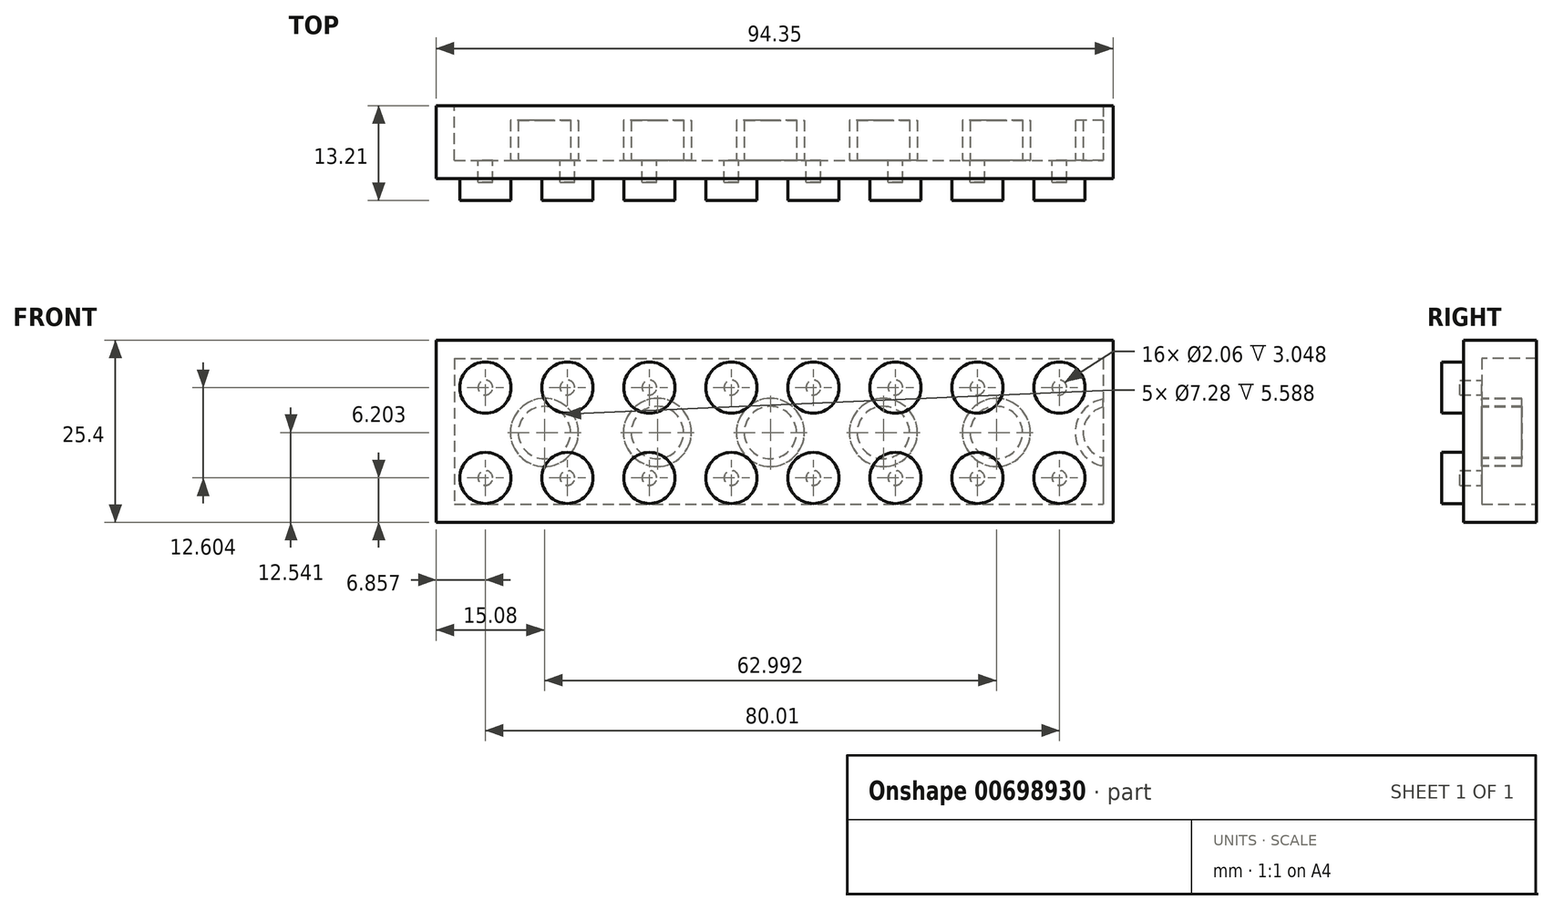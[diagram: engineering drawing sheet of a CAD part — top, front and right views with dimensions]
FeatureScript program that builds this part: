
annotation { "Feature Type Name" : "Feature", "Feature Type Description" : "" }
export const myFeature = defineFeature(function(context is Context, id is Id, definition is map)
    precondition{}
    {
        {
            var Q0;
            Q0=qCreatedBy(makeId("Front.planeOp"),FACE);
            var sketch = newSketch(context, id + "F0", { "sketchPlane" : qUnion([Q0])});
            skLineSegment(sketch, "E0.bottom", {"start": v(-52.92, 48.52) * mm, "end": v(74.08, 48.52) * mm});
            skLineSegment(sketch, "E0.top", {"start": v(-52.92, 23.12) * mm, "end": v(74.08, 23.12) * mm});
            skLineSegment(sketch, "E0.left", {"start": v(-52.92, 48.52) * mm, "end": v(-52.92, 23.12) * mm});
            skLineSegment(sketch, "E0.right", {"start": v(74.08, 48.52) * mm, "end": v(74.08, 23.12) * mm});
            skSolve(sketch);
        }
        {
            var Q0;
            Q0 = qSketchRegion(id + "F0", true);
            extrude(context, id + "F1", {"entities" : qUnion([Q0]), "depth" : 10.16 * mm, "offsetDistance" : 25.4 * mm});
        }
        {
            var Q0;
            Q0=makeQuery(id+"F1.opExtrude","CAP_FACE",FACE,{"disambiguationData":[OSD([sQuery(id+"F0.wireOp",EDGE,"E0.bottom"),sQuery(id+"F0.wireOp",EDGE,"E0.top"),sQuery(id+"F0.wireOp",EDGE,"E0.left"),sQuery(id+"F0.wireOp",EDGE,"E0.right")])],"isStart":false});
            var sketch = newSketch(context, id + "F2", { "sketchPlane" : qUnion([Q0])});
            skCircle(sketch, "E1", {"center": v(-46.06, 41.93) * mm, "radius": 3.57 * mm});
            skCircle(sketch, "E2", {"center": v(-46.06, 29.32) * mm, "radius": 3.57 * mm});
            skLineSegment(sketch, "E3.direction1", {"start": v(-46.06, 41.93) * mm, "end": v(-30.32, 41.93) * mm, "construction": true});
            skLineSegment(sketch, "E4", {"start": v(-34.2, 48.52) * mm, "end": v(-33.78, 23.12) * mm});
            skCircle(sketch, "E5.1.0.0", {"center": v(-34.63, 41.93) * mm, "radius": 3.57 * mm});
            skCircle(sketch, "E5.1.0.1", {"center": v(-34.63, 29.32) * mm, "radius": 3.57 * mm});
            skCircle(sketch, "E5.2.0.0", {"center": v(-23.2, 41.93) * mm, "radius": 3.57 * mm});
            skCircle(sketch, "E5.2.0.1", {"center": v(-23.2, 29.32) * mm, "radius": 3.57 * mm});
            skCircle(sketch, "E5.3.0.0", {"center": v(-11.77, 41.93) * mm, "radius": 3.57 * mm});
            skCircle(sketch, "E5.3.0.1", {"center": v(-11.77, 29.32) * mm, "radius": 3.57 * mm});
            skCircle(sketch, "E5.4.0.0", {"center": v(-0.34, 41.93) * mm, "radius": 3.57 * mm});
            skCircle(sketch, "E5.4.0.1", {"center": v(-0.34, 29.32) * mm, "radius": 3.57 * mm});
            skCircle(sketch, "E5.5.0.0", {"center": v(11.09, 41.93) * mm, "radius": 3.57 * mm});
            skCircle(sketch, "E5.5.0.1", {"center": v(11.09, 29.32) * mm, "radius": 3.57 * mm});
            skCircle(sketch, "E5.6.0.0", {"center": v(22.52, 41.93) * mm, "radius": 3.57 * mm});
            skCircle(sketch, "E5.6.0.1", {"center": v(22.52, 29.32) * mm, "radius": 3.57 * mm});
            skCircle(sketch, "E5.7.0.0", {"center": v(33.95, 41.93) * mm, "radius": 3.57 * mm});
            skCircle(sketch, "E5.7.0.1", {"center": v(33.95, 29.32) * mm, "radius": 3.57 * mm});
            skLineSegment(sketch, "E5.direction1", {"start": v(-46.06, 41.93) * mm, "end": v(-34.63, 41.93) * mm, "construction": true});
            skSolve(sketch);
        }
        {
            var Q0;
            Q0 = qSketchRegion(id + "F2", true);
            extrude(context, id + "F3", {"entities" : qUnion([Q0]), "operationType" : NewBodyOperationType.ADD, "depth" : 3.05 * mm, "offsetDistance" : 25.4 * mm});
        }
        {
            var Q0;
            Q0=makeQuery(id+"F1.opExtrude","CAP_FACE",FACE,{"disambiguationData":[OSD([sQuery(id+"F0.wireOp",EDGE,"E0.bottom"),sQuery(id+"F0.wireOp",EDGE,"E0.top"),sQuery(id+"F0.wireOp",EDGE,"E0.left"),sQuery(id+"F0.wireOp",EDGE,"E0.right")])],"isStart":true});
            shell(context, id + "F4", {"entities" : qUnion([Q0]), "thickness" : 2.54 * mm});
        }
        {
            var Q0;
            Q0=makeQuery(id+"F4.opShell","OFFSET_FACE",FACE,{"disambiguationData":[OSD([sQuery(id+"F0.wireOp",EDGE,"E0.bottom"),sQuery(id+"F0.wireOp",EDGE,"E0.top"),sQuery(id+"F0.wireOp",EDGE,"E0.left"),sQuery(id+"F0.wireOp",EDGE,"E0.right")])]});
            var sketch = newSketch(context, id + "F5", { "sketchPlane" : qUnion([Q0])});
            skCircle(sketch, "E6", {"center": v(37.84, 35.66) * mm, "radius": 4.74 * mm});
            skCircle(sketch, "E7", {"center": v(37.84, 35.66) * mm, "radius": 3.64 * mm});
            skCircle(sketch, "E8.1.0.0", {"center": v(22.1, 35.66) * mm, "radius": 3.64 * mm});
            skCircle(sketch, "E8.1.0.1", {"center": v(22.1, 35.66) * mm, "radius": 4.74 * mm});
            skCircle(sketch, "E8.2.0.0", {"center": v(6.34, 35.66) * mm, "radius": 3.64 * mm});
            skCircle(sketch, "E8.2.0.1", {"center": v(6.34, 35.66) * mm, "radius": 4.74 * mm});
            skCircle(sketch, "E8.3.0.0", {"center": v(-9.4, 35.66) * mm, "radius": 3.64 * mm});
            skCircle(sketch, "E8.3.0.1", {"center": v(-9.4, 35.66) * mm, "radius": 4.74 * mm});
            skCircle(sketch, "E8.4.0.0", {"center": v(-25.15, 35.66) * mm, "radius": 3.64 * mm});
            skCircle(sketch, "E8.4.0.1", {"center": v(-25.15, 35.66) * mm, "radius": 4.74 * mm});
            skCircle(sketch, "E8.5.0.0", {"center": v(-40.9, 35.66) * mm, "radius": 3.64 * mm});
            skCircle(sketch, "E8.5.0.1", {"center": v(-40.9, 35.66) * mm, "radius": 4.74 * mm});
            skCircle(sketch, "E8.6.0.0", {"center": v(-56.65, 35.66) * mm, "radius": 3.64 * mm});
            skCircle(sketch, "E8.6.0.1", {"center": v(-56.65, 35.66) * mm, "radius": 4.74 * mm});
            skLineSegment(sketch, "E8.direction1", {"start": v(37.84, 35.66) * mm, "end": v(22.1, 35.66) * mm, "construction": true});
            skSolve(sketch);
        }
        {
            var Q0;
            Q0 = qSketchRegion(id + "F5", true);
            extrude(context, id + "F6", {"entities" : qUnion([Q0]), "operationType" : NewBodyOperationType.ADD, "depth" : 5.6 * mm, "offsetDistance" : 25.4 * mm});
        }
        {
            var Q0;
            Q0=makeQuery(id+"F1.opExtrude","CAP_FACE",FACE,{"disambiguationData":[OSD([sQuery(id+"F0.wireOp",EDGE,"E0.bottom"),sQuery(id+"F0.wireOp",EDGE,"E0.top"),sQuery(id+"F0.wireOp",EDGE,"E0.left"),sQuery(id+"F0.wireOp",EDGE,"E0.right")])],"isStart":false});
            var sketch = newSketch(context, id + "F7", { "sketchPlane" : qUnion([Q0])});
            skLineSegment(sketch, "E9", {"start": v(40.06, 48.52) * mm, "end": v(40.06, 23.12) * mm});
            skLineSegment(sketch, "E10", {"start": v(40.06, 23.12) * mm, "end": v(74.08, 23.12) * mm});
            skLineSegment(sketch, "E11", {"start": v(74.08, 23.12) * mm, "end": v(74.08, 48.52) * mm});
            skLineSegment(sketch, "E12", {"start": v(74.08, 48.52) * mm, "end": v(40.06, 48.52) * mm});
            skSolve(sketch);
        }
        {
            var Q0;
            Q0 = qSketchRegion(id + "F7", true);
            extrude(context, id + "F8", {"entities" : qUnion([Q0]), "operationType" : NewBodyOperationType.REMOVE, "oppositeDirection" : true, "depth" : 25.4 * mm, "offsetDistance" : 25.4 * mm});
        }
        {
            var Q0;
            Q0=makeQuery(id+"F8.boolean.opBoolean","COPY",FACE,{"derivedFrom":makeQuery(id+"F8.opExtrude","SWEPT_FACE",FACE,{"disambiguationData":[OSD([sQuery(id+"F7.wireOp",EDGE,"E9")])]})});
            var sketch = newSketch(context, id + "F9", { "sketchPlane" : qUnion([Q0])});
            skLineSegment(sketch, "E13", {"start": v(-10.16, 48.52) * mm, "end": v(0, 48.52) * mm});
            skLineSegment(sketch, "E14", {"start": v(0, 48.52) * mm, "end": v(0, 23.12) * mm});
            skLineSegment(sketch, "E15", {"start": v(0, 23.12) * mm, "end": v(-10.16, 23.12) * mm});
            skLineSegment(sketch, "E16", {"start": v(-10.16, 23.12) * mm, "end": v(-10.16, 48.52) * mm});
            skSolve(sketch);
        }
        {
            var Q0;
            Q0 = qSketchRegion(id + "F9", true);
            extrude(context, id + "F10", {"entities" : qUnion([Q0]), "operationType" : NewBodyOperationType.ADD, "depth" : 1.37 * mm, "offsetDistance" : 25.4 * mm});
        }
    });
